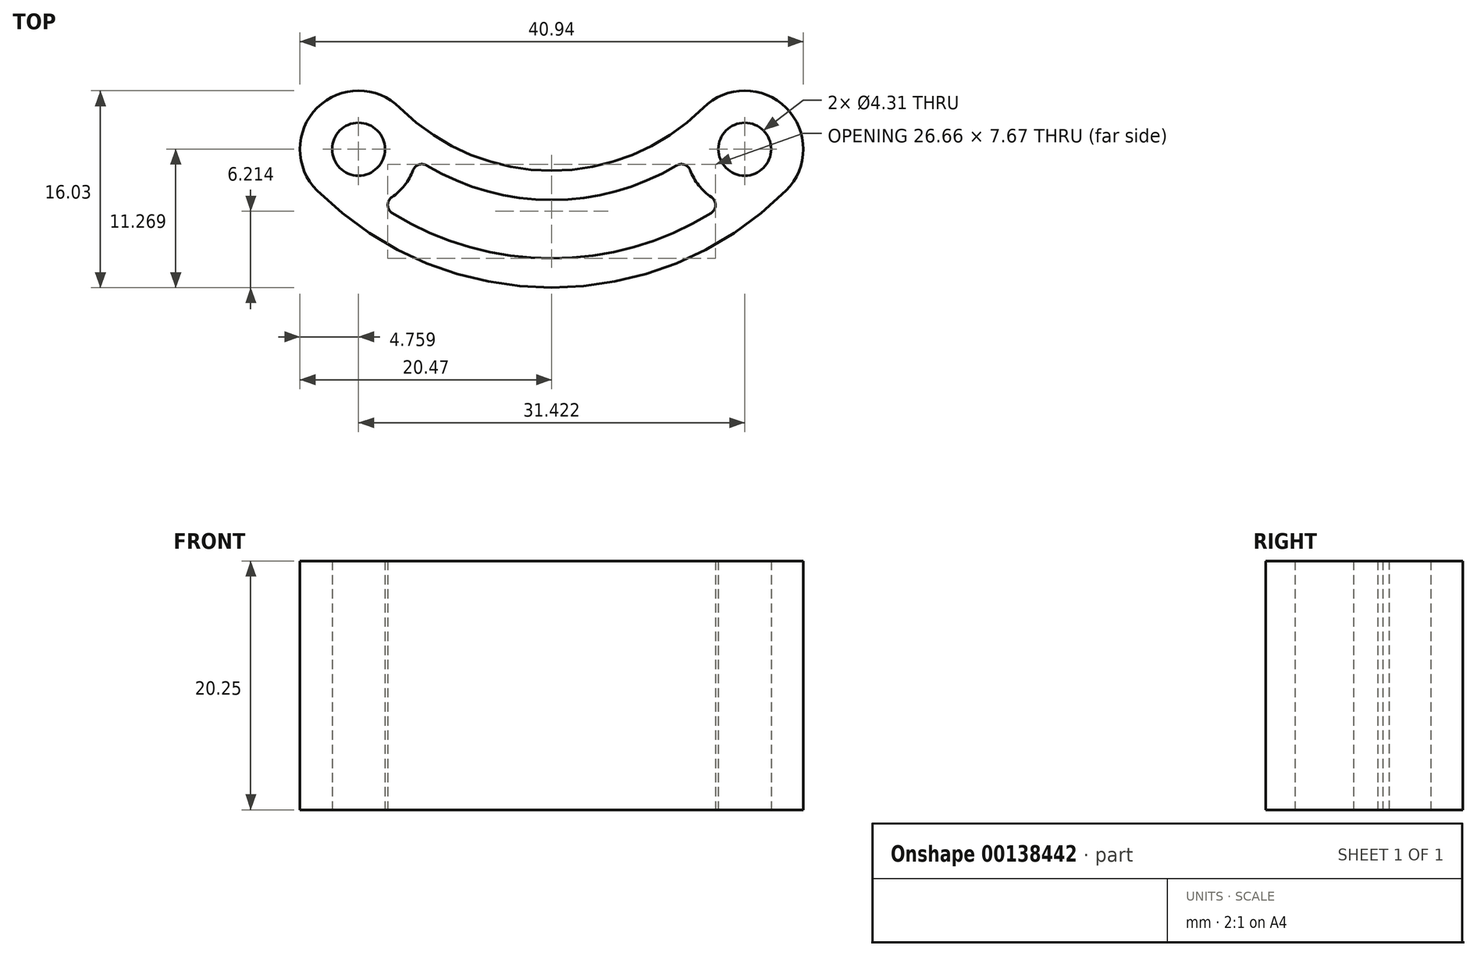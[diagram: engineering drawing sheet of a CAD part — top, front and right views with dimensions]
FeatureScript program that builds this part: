
annotation { "Feature Type Name" : "Feature", "Feature Type Description" : "" }
export const myFeature = defineFeature(function(context is Context, id is Id, definition is map)
    precondition{}
    {
        {
            var Q0;
            Q0=qCreatedBy(makeId("Top.planeOp"),FACE);
            var sketch = newSketch(context, id + "F0", { "sketchPlane" : qUnion([Q0])});
            skLineSegment(sketch, "E0", {"start": v(0, 0) * mm, "end": v(0, -15.71) * mm, "construction": true});
            skLineSegment(sketch, "E1", {"start": v(-15.71, -15.71) * mm, "end": v(15.71, -15.71) * mm, "construction": true});
            skLineSegment(sketch, "E2", {"start": v(0, 0) * mm, "end": v(15.71, -15.71) * mm, "construction": true});
            skCircle(sketch, "E3", {"center": v(-15.71, -15.71) * mm, "radius": 2.15 * mm});
            skCircle(sketch, "E4", {"center": v(15.71, -15.71) * mm, "radius": 2.15 * mm});
            skArc(sketch, "E5", {"start": v(-12.34, -12.34) * mm, "mid": v(-19.08, -12.34) * mm, "end": v(-19.08, -19.08) * mm});
            skArc(sketch, "E6", {"start": v(19.08, -19.08) * mm, "mid": v(19.08, -12.34) * mm, "end": v(12.34, -12.34) * mm});
            skArc(sketch, "E7", {"start": v(-19.08, -19.08) * mm, "mid": v(0, -26.98) * mm, "end": v(19.08, -19.08) * mm});
            skArc(sketch, "E8", {"start": v(-12.34, -12.34) * mm, "mid": v(0, -17.46) * mm, "end": v(12.34, -12.34) * mm});
            skArc(sketch, "E9", {"start": v(-14.07, -20.18) * mm, "mid": v(-12.05, -18.75) * mm, "end": v(-11.01, -16.5) * mm});
            skArc(sketch, "E10", {"start": v(-11.01, -16.5) * mm, "mid": v(0, -19.84) * mm, "end": v(11.01, -16.5) * mm});
            skArc(sketch, "E11", {"start": v(11.01, -16.5) * mm, "mid": v(12.05, -18.75) * mm, "end": v(14.07, -20.18) * mm});
            skArc(sketch, "E12", {"start": v(-14.07, -20.18) * mm, "mid": v(0, -24.6) * mm, "end": v(14.07, -20.18) * mm});
            skSolve(sketch);
        }
        {
            var Q0;
            Q0=qSketchRegion(id+"F0",true);
            extrude(context, id + "F1", {"entities" : qUnion([Q0]), "depth" : 20.25 * mm});
        }
        {
            var Q0;
            Q0=makeQuery(id+"F1.opExtrude","SWEPT_EDGE",EDGE,{"disambiguationData":[OSD([sQuery(id+"F0.wireOp",EDGE,"E9"),sQuery(id+"F0.wireOp",EDGE,"E10")])]});
            var Q1;
            Q1=makeQuery(id+"F1.opExtrude","SWEPT_EDGE",EDGE,{"disambiguationData":[OSD([sQuery(id+"F0.wireOp",EDGE,"E9"),sQuery(id+"F0.wireOp",EDGE,"E12")])]});
            var Q2;
            Q2=makeQuery(id+"F1.opExtrude","SWEPT_EDGE",EDGE,{"disambiguationData":[OSD([sQuery(id+"F0.wireOp",EDGE,"E10"),sQuery(id+"F0.wireOp",EDGE,"E11")])]});
            var Q3;
            Q3=makeQuery(id+"F1.opExtrude","SWEPT_EDGE",EDGE,{"disambiguationData":[OSD([sQuery(id+"F0.wireOp",EDGE,"E11"),sQuery(id+"F0.wireOp",EDGE,"E12")])]});
            fillet(context, id + "F2", {"entities" : qUnion([Q0, Q1, Q2, Q3]), "radius" : 0.76 * mm, "tangentPropagation" : true, "allowEdgeOverflow" : false});
        }
    });
